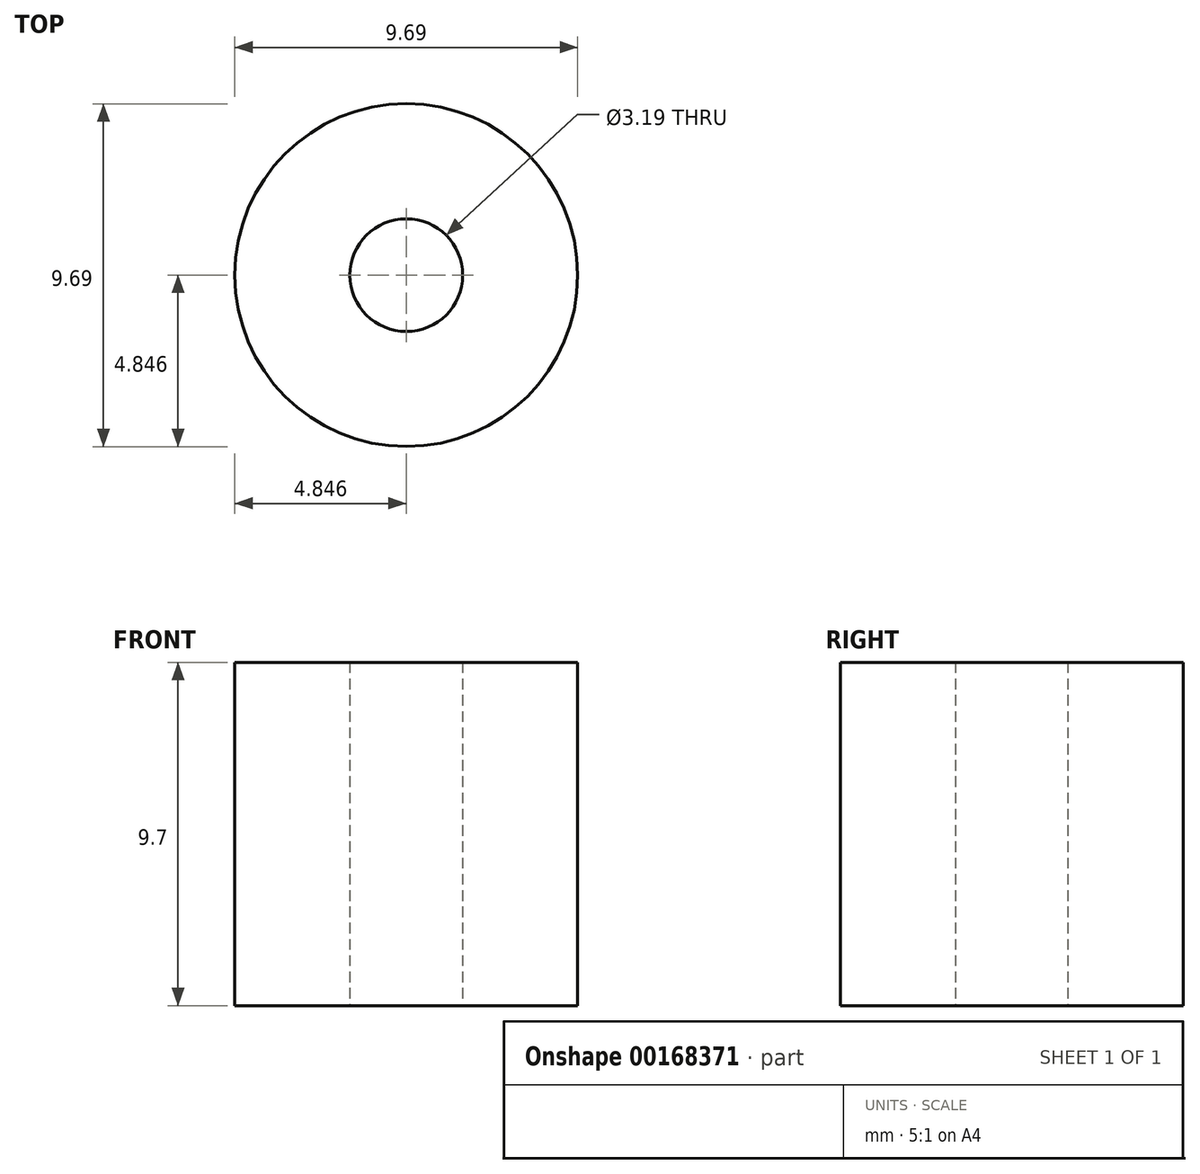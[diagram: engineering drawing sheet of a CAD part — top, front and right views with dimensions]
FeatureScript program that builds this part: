
annotation { "Feature Type Name" : "Feature", "Feature Type Description" : "" }
export const myFeature = defineFeature(function(context is Context, id is Id, definition is map)
    precondition{}
    {
        {
            var Q0;
            Q0=qCreatedBy(makeId("Top.planeOp"),FACE);
            var sketch = newSketch(context, id + "F0", { "sketchPlane" : qUnion([Q0])});
            skCircle(sketch, "E0", {"center": v(-47.5, 41.96) * mm, "radius": 4.84 * mm});
            skCircle(sketch, "E1", {"center": v(-47.5, 41.96) * mm, "radius": 1.6 * mm});
            skSolve(sketch);
        }
        {
            var Q0;
            Q0=makeQuery(id+"F0.imprint","IMPRINT",FACE,{"disambiguationData":[TD([[makeQuery(id+"F0.imprint","IMPRINT",EDGE,{"derivedFrom":sQuery(id+"F0.wireOp",EDGE,"E0")}),1.0]])]});
            extrude(context, id + "F1", {"entities" : qUnion([Q0]), "depth" : 9.7 * mm});
        }
    });
